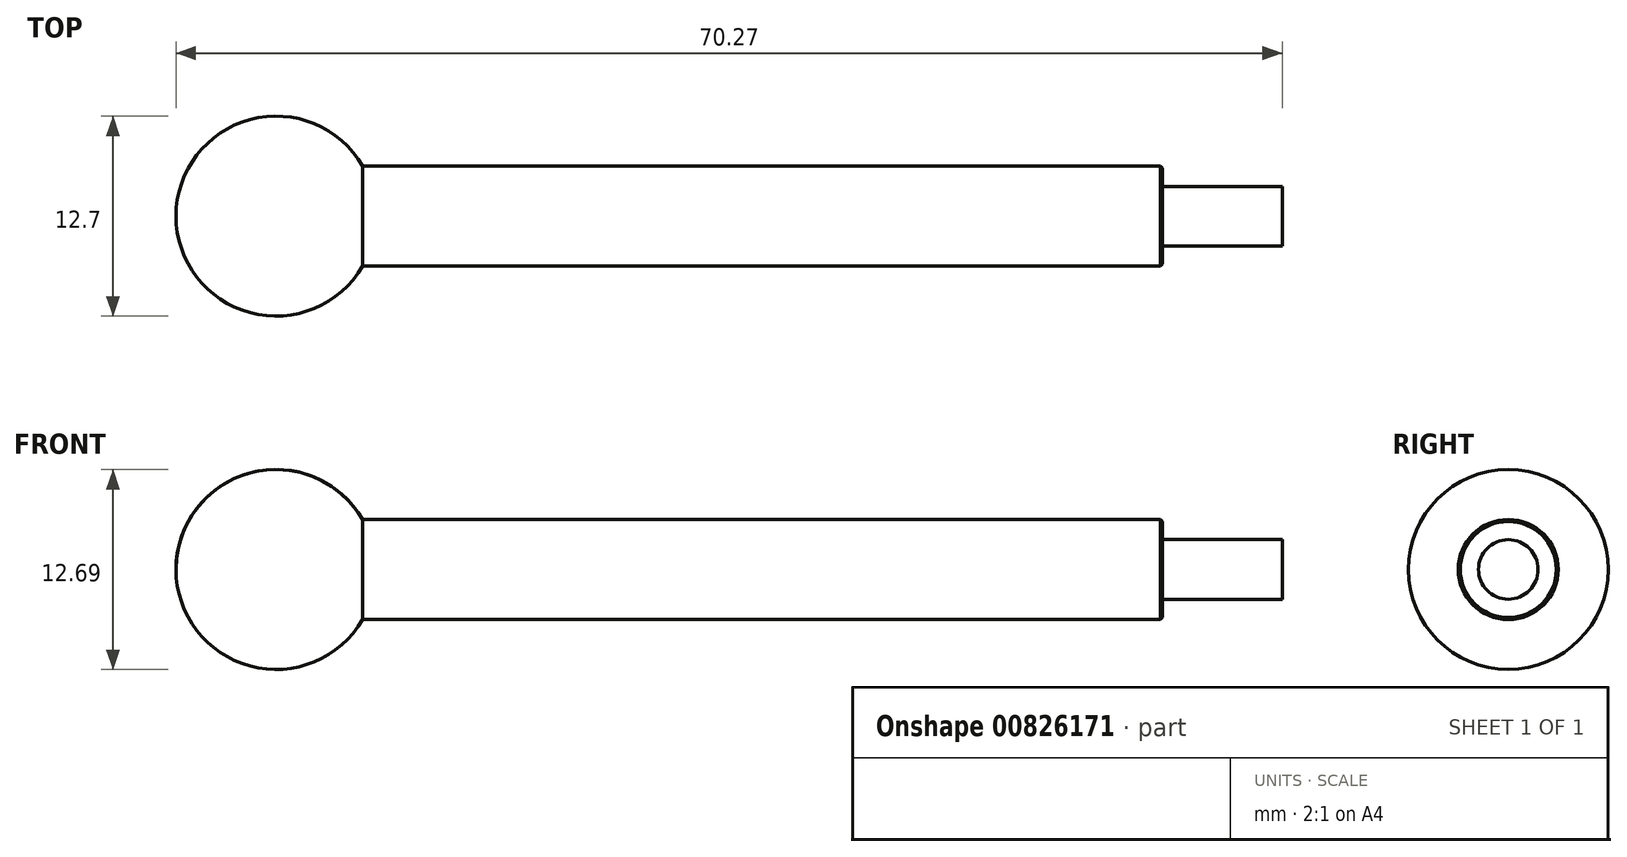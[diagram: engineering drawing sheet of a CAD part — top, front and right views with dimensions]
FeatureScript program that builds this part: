
annotation { "Feature Type Name" : "Feature", "Feature Type Description" : "" }
export const myFeature = defineFeature(function(context is Context, id is Id, definition is map)
    precondition{}
    {
        {
            var Q0;
            Q0=qCreatedBy(makeId("Front.planeOp"),FACE);
            var sketch = newSketch(context, id + "F0", { "sketchPlane" : qUnion([Q0])});
            skLineSegment(sketch, "E0", {"start": v(0, 0) * mm, "end": v(50.8, 0) * mm});
            skLineSegment(sketch, "E1", {"start": v(0, 6.35) * mm, "end": v(50.8, 6.35) * mm});
            skLineSegment(sketch, "E2", {"start": v(50.8, 6.35) * mm, "end": v(50.8, 14.35) * mm, "construction": true});
            skLineSegment(sketch, "E3", {"start": v(50.8, 0) * mm, "end": v(50.8, -8.24) * mm, "construction": true});
            skArc(sketch, "E4", {"start": v(0, 6.35) * mm, "mid": v(-11.85, 3.17) * mm, "end": v(0, 0) * mm});
            skLineSegment(sketch, "E5", {"start": v(50.8, 6.35) * mm, "end": v(50.8, 5.07) * mm});
            skLineSegment(sketch, "E6", {"start": v(50.8, 5.07) * mm, "end": v(58.42, 5.07) * mm});
            skLineSegment(sketch, "E7", {"start": v(58.42, 5.07) * mm, "end": v(58.42, 1.27) * mm});
            skLineSegment(sketch, "E8", {"start": v(58.42, 1.27) * mm, "end": v(50.8, 1.27) * mm});
            skLineSegment(sketch, "E9", {"start": v(50.8, 1.27) * mm, "end": v(50.8, 0) * mm});
            skLineSegment(sketch, "E10", {"start": v(-27.7, 3.17) * mm, "end": v(94.16, 3.18) * mm, "construction": true});
            skLineSegment(sketch, "E11", {"start": v(-11.85, 3.17) * mm, "end": v(-20.98, 3.17) * mm});
            skLineSegment(sketch, "E12", {"start": v(-20.98, 3.17) * mm, "end": v(-20.98, 20.08) * mm});
            skLineSegment(sketch, "E13", {"start": v(-20.98, 20.08) * mm, "end": v(59.18, 20.08) * mm});
            skLineSegment(sketch, "E14", {"start": v(59.18, 20.08) * mm, "end": v(58.42, 5.07) * mm});
            skSolve(sketch);
        }
        {
            var Q0;
            Q0=makeQuery(id+"F0.imprint","IMPRINT",FACE,{"disambiguationData":[TD([[makeQuery(id+"F0.imprint","IMPRINT",EDGE,{"derivedFrom":sQuery(id+"F0.wireOp",EDGE,"E0")}),1.0]])]});
            extrude(context, id + "F1", {"entities" : qUnion([Q0]), "endBound" : BoundingType.SYMMETRIC, "depth" : 12.7 * mm, "offsetDistance" : 25.4 * mm});
        }
        {
            var Q0;
            {var subQ1=sQuery(id+"F0.wireOp",EDGE,"E1");Q0=makeQuery(id+"F0.imprint","IMPRINT",FACE,{"disambiguationData":[TD([[makeQuery(id+"F0.imprint","IMPRINT",EDGE,{"derivedFrom":subQ1}),1.0]])]});}
            var Q1;
            Q1=sQuery(id+"F0.wireOp",EDGE,"E10");
            revolve(context, id + "F2", {"operationType" : NewBodyOperationType.REMOVE, "surfaceOperationType" : NewSurfaceOperationType.NEW, "entities" : qUnion([Q0]), "axis" : qUnion([Q1]), "revolveType" : RevolveType.FULL, "oppositeDirection" : true});
        }
        {
            var Q0;
            Q0=makeQuery(id+"F2.boolean.opBoolean","COPY",EDGE,{"derivedFrom":makeQuery(id+"F2.opRevolve","SWEPT_EDGE",EDGE,{"disambiguationData":[OSD([sQuery(id+"F0.wireOp",EDGE,"E6"),sQuery(id+"F0.wireOp",EDGE,"E7"),sQuery(id+"F0.wireOp",EDGE,"E14")])]})});
            var Q1;
            {var subQ0=sQuery(id+"F0.wireOp",EDGE,"E5");Q1=makeQuery(id+"F2.boolean.opBoolean","INTERSECT",EDGE,{"derivedFrom":[makeQuery(id+"F1.opExtrude","SWEPT_FACE",FACE,{"disambiguationData":[OSD([subQ0])]}),makeQuery(id+"F1.opExtrude","SWEPT_FACE",FACE,{"disambiguationData":[OSD([sQuery(id+"F0.wireOp",EDGE,"E9")])]}),makeQuery(id+"F2.opRevolve","SWEPT_FACE",FACE,{"disambiguationData":[OSD([subQ0])]})]});}
            chamfer(context, id + "F3", {"entities" : qUnion([Q0, Q1]), "width" : 0.13 * mm, "tangentPropagation" : true});
        }
        {
            var Q0;
            Q0=makeQuery(id+"F2.boolean.opBoolean","COPY",EDGE,{"derivedFrom":makeQuery(id+"F2.opRevolve","SWEPT_EDGE",EDGE,{"disambiguationData":[OSD([sQuery(id+"F0.wireOp",EDGE,"E5"),sQuery(id+"F0.wireOp",EDGE,"E6")])]})});
            fillet(context, id + "F4", {"entities" : qUnion([Q0]), "radius" : 0.13 * mm, "tangentPropagation" : true, "allowEdgeOverflow" : false});
        }
    });
